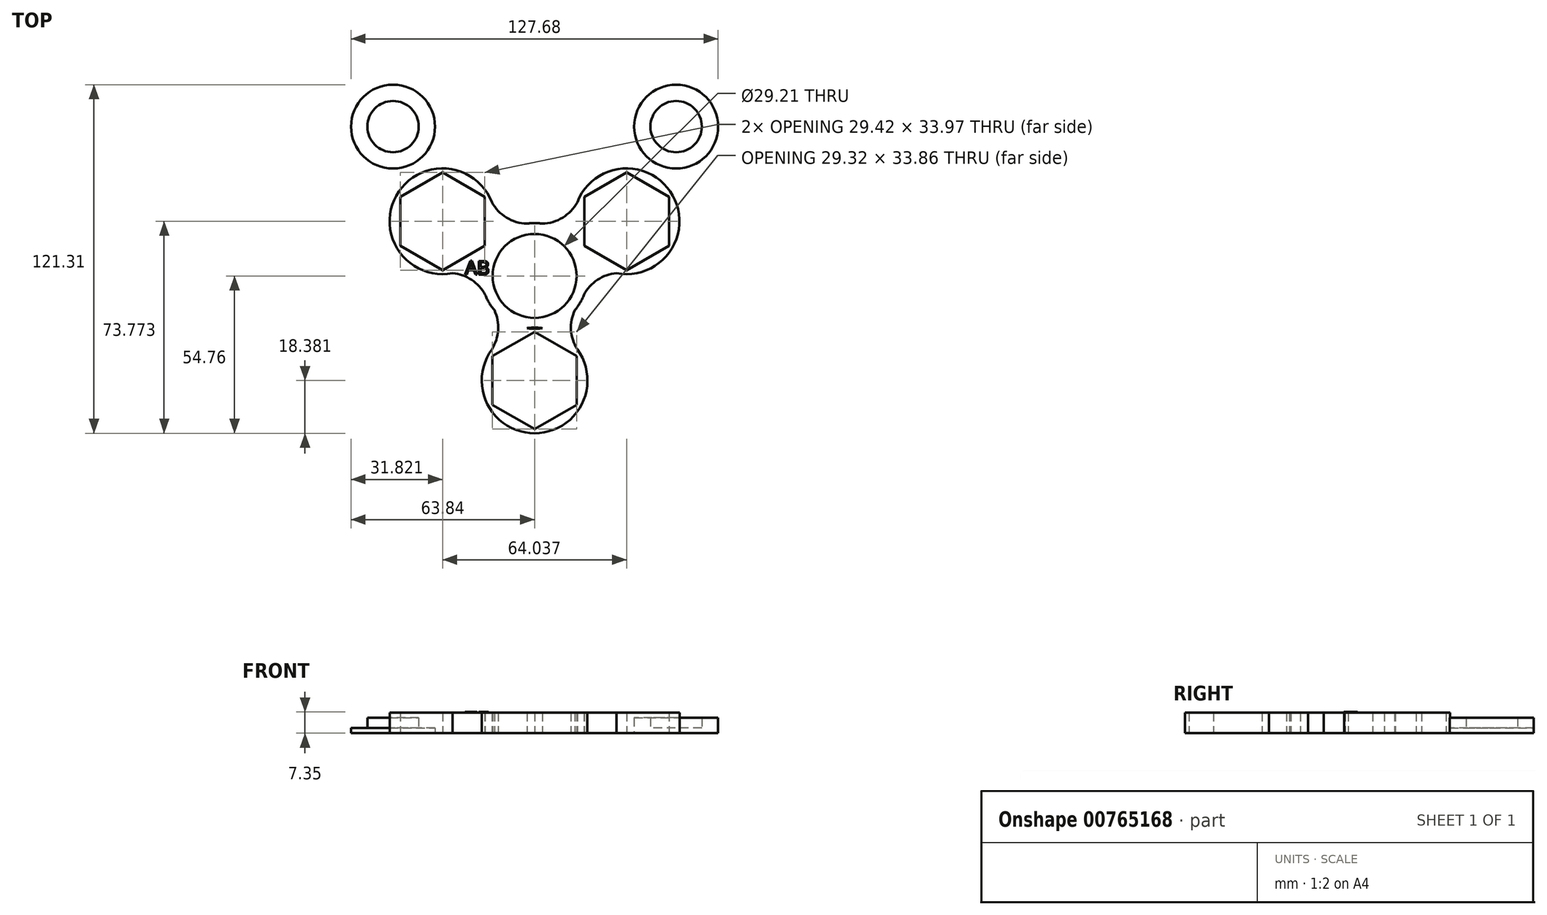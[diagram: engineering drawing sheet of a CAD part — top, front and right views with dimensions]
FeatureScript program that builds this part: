
annotation { "Feature Type Name" : "Feature", "Feature Type Description" : "" }
export const myFeature = defineFeature(function(context is Context, id is Id, definition is map)
    precondition{}
    {
        {
            var Q0;
            Q0=qCreatedBy(makeId("Top.planeOp"),FACE);
            var sketch = newSketch(context, id + "F0", { "sketchPlane" : qUnion([Q0])});
            skCircle(sketch, "E0", {"center": v(0, 0) * mm, "radius": 14.6 * mm});
            skPoint(sketch, "E1", {"position": v(32.02, 19.01) * mm});
            skPoint(sketch, "E2.MirrorP", {"position": v(-32.02, 19.01) * mm});
            skCircle(sketch, "E3", {"center": v(0, 0) * mm, "radius": 18.39 * mm});
            skCircle(sketch, "E4", {"center": v(-32.02, 19.01) * mm, "radius": 18.39 * mm});
            skCircle(sketch, "E5", {"center": v(32.02, 19.01) * mm, "radius": 18.39 * mm});
            skCircle(sketch, "E6", {"center": v(0, -36.38) * mm, "radius": 18.39 * mm});
            skLineSegment(sketch, "E7.0", {"start": v(-17.3, 27.5) * mm, "end": v(-17.3, 10.52) * mm});
            skLineSegment(sketch, "E7.1", {"start": v(-17.3, 10.52) * mm, "end": v(-32.02, 2.03) * mm});
            skLineSegment(sketch, "E7.2", {"start": v(-32.02, 2.03) * mm, "end": v(-46.73, 10.52) * mm});
            skLineSegment(sketch, "E7.3", {"start": v(-46.73, 10.52) * mm, "end": v(-46.73, 27.5) * mm});
            skLineSegment(sketch, "E7.4", {"start": v(-46.73, 27.5) * mm, "end": v(-32.02, 36) * mm});
            skLineSegment(sketch, "E7.5", {"start": v(-32.02, 36) * mm, "end": v(-17.3, 27.5) * mm});
            skPoint(sketch, "E7.0.midPoint", {"position": v(-17.3, 19.01) * mm});
            skLineSegment(sketch, "E8.0", {"start": v(46.73, 27.5) * mm, "end": v(46.73, 10.52) * mm});
            skLineSegment(sketch, "E8.1", {"start": v(46.73, 10.52) * mm, "end": v(32.02, 2.03) * mm});
            skLineSegment(sketch, "E8.2", {"start": v(32.02, 2.03) * mm, "end": v(17.3, 10.52) * mm});
            skLineSegment(sketch, "E8.3", {"start": v(17.3, 10.52) * mm, "end": v(17.3, 27.5) * mm});
            skLineSegment(sketch, "E8.4", {"start": v(17.3, 27.5) * mm, "end": v(32.02, 36) * mm});
            skLineSegment(sketch, "E8.5", {"start": v(32.02, 36) * mm, "end": v(46.73, 27.5) * mm});
            skPoint(sketch, "E8.0.midPoint", {"position": v(46.73, 19.01) * mm});
            skLineSegment(sketch, "E9.0", {"start": v(14.66, -27.91) * mm, "end": v(14.66, -44.84) * mm});
            skLineSegment(sketch, "E9.1", {"start": v(14.66, -44.84) * mm, "end": v(0, -53.3) * mm});
            skLineSegment(sketch, "E9.2", {"start": v(0, -53.3) * mm, "end": v(-14.66, -44.84) * mm});
            skLineSegment(sketch, "E9.3", {"start": v(-14.66, -44.84) * mm, "end": v(-14.66, -27.91) * mm});
            skLineSegment(sketch, "E9.4", {"start": v(-14.66, -27.91) * mm, "end": v(0, -19.45) * mm});
            skLineSegment(sketch, "E9.5", {"start": v(0, -19.45) * mm, "end": v(14.66, -27.91) * mm});
            skPoint(sketch, "E9.0.midPoint", {"position": v(14.66, -36.38) * mm});
            skArc(sketch, "E10", {"start": v(-15.71, 27.5) * mm, "mid": v(-9.5, 20.11) * mm, "end": v(0, 18.39) * mm});
            skArc(sketch, "E11.MirrorCS", {"start": v(15.71, 27.5) * mm, "mid": v(9.5, 20.11) * mm, "end": v(0, 18.39) * mm});
            skArc(sketch, "E12", {"start": v(32.94, 0.65) * mm, "mid": v(22.96, -0.71) * mm, "end": v(16.39, -8.34) * mm});
            skArc(sketch, "E13", {"start": v(16.39, -8.34) * mm, "mid": v(12.67, -17.25) * mm, "end": v(15.5, -26.48) * mm});
            skArc(sketch, "E14.MirrorCS", {"start": v(-32.94, 0.65) * mm, "mid": v(-22.96, -0.71) * mm, "end": v(-16.39, -8.34) * mm});
            skArc(sketch, "E15.MirrorCS", {"start": v(-16.39, -8.34) * mm, "mid": v(-12.67, -17.25) * mm, "end": v(-15.5, -26.48) * mm});
            skSolve(sketch);
        }
        {
            var Q0;
            Q0=qCreatedBy(makeId("Top.planeOp"),FACE);
            var sketch = newSketch(context, id + "F1", { "sketchPlane" : qUnion([Q0])});
            skCircle(sketch, "E16", {"center": v(-49.24, 51.95) * mm, "radius": 8.93 * mm});
            skCircle(sketch, "E17.MirrorC", {"center": v(49.24, 51.95) * mm, "radius": 8.93 * mm});
            skCircle(sketch, "E18", {"center": v(-49.24, 51.95) * mm, "radius": 14.6 * mm});
            skCircle(sketch, "E19", {"center": v(49.24, 51.95) * mm, "radius": 14.6 * mm});
            skSolve(sketch);
        }
        {
            var Q0;
            Q0 = qSketchRegion(id + "F0", true);
            extrude(context, id + "F2", {"entities" : qUnion([Q0]), "depth" : 7.11 * mm, "offsetDistance" : 25.4 * mm});
        }
        {
            var Q0;
            Q0=makeQuery(id+"F1.imprint","IMPRINT",FACE,{"disambiguationData":[TD([[makeQuery(id+"F1.imprint","IMPRINT",EDGE,{"derivedFrom":sQuery(id+"F1.wireOp",EDGE,"E16")}),1.0]])]});
            extrude(context, id + "F3", {"entities" : qUnion([Q0]), "depth" : 5.33 * mm, "offsetDistance" : 25.4 * mm});
        }
        {
            var Q0;
            Q0=makeQuery(id+"F1.imprint","IMPRINT",FACE,{"disambiguationData":[TD([[makeQuery(id+"F1.imprint","IMPRINT",EDGE,{"derivedFrom":sQuery(id+"F1.wireOp",EDGE,"E17.MirrorC")}),-1.0]])]});
            extrude(context, id + "F4", {"entities" : qUnion([Q0]), "depth" : 5.33 * mm, "offsetDistance" : 25.4 * mm});
        }
        {
            var Q0;
            Q0=makeQuery(id+"F1.imprint","IMPRINT",FACE,{"disambiguationData":[TD([[makeQuery(id+"F1.imprint","IMPRINT",EDGE,{"derivedFrom":sQuery(id+"F1.wireOp",EDGE,"E16")}),-1.0]])]});
            extrude(context, id + "F5", {"entities" : qUnion([Q0]), "operationType" : NewBodyOperationType.ADD, "depth" : 1.78 * mm, "offsetDistance" : 25.4 * mm});
        }
        {
            var Q0;
            Q0=makeQuery(id+"F1.imprint","IMPRINT",FACE,{"disambiguationData":[TD([[makeQuery(id+"F1.imprint","IMPRINT",EDGE,{"derivedFrom":sQuery(id+"F1.wireOp",EDGE,"E17.MirrorC")}),1.0]])]});
            extrude(context, id + "F6", {"entities" : qUnion([Q0]), "operationType" : NewBodyOperationType.ADD, "depth" : 1.78 * mm, "offsetDistance" : 25.4 * mm});
        }
        {
            var Q0;
            Q0=qCreatedBy(makeId("Top.planeOp"),FACE);
            var sketch = newSketch(context, id + "F7", { "sketchPlane" : qUnion([Q0])});
            skText(sketch, "E20", { "text": "AB", "fontName": "OpenSans-Regular.ttf"});
            const initialGuessF7  = {"E20": [-0.0242, 0.00045, 1, 0, 0.0048]};
            skSetInitialGuess(sketch, initialGuessF7);
            skSolve(sketch);
        }
        {
            var Q0;
            Q0 = qSketchRegion(id + "F7", true);
            extrude(context, id + "F8", {"entities" : qUnion([Q0]), "operationType" : NewBodyOperationType.ADD, "depth" : 7.35 * mm, "offsetDistance" : 25 * mm});
        }
    });
